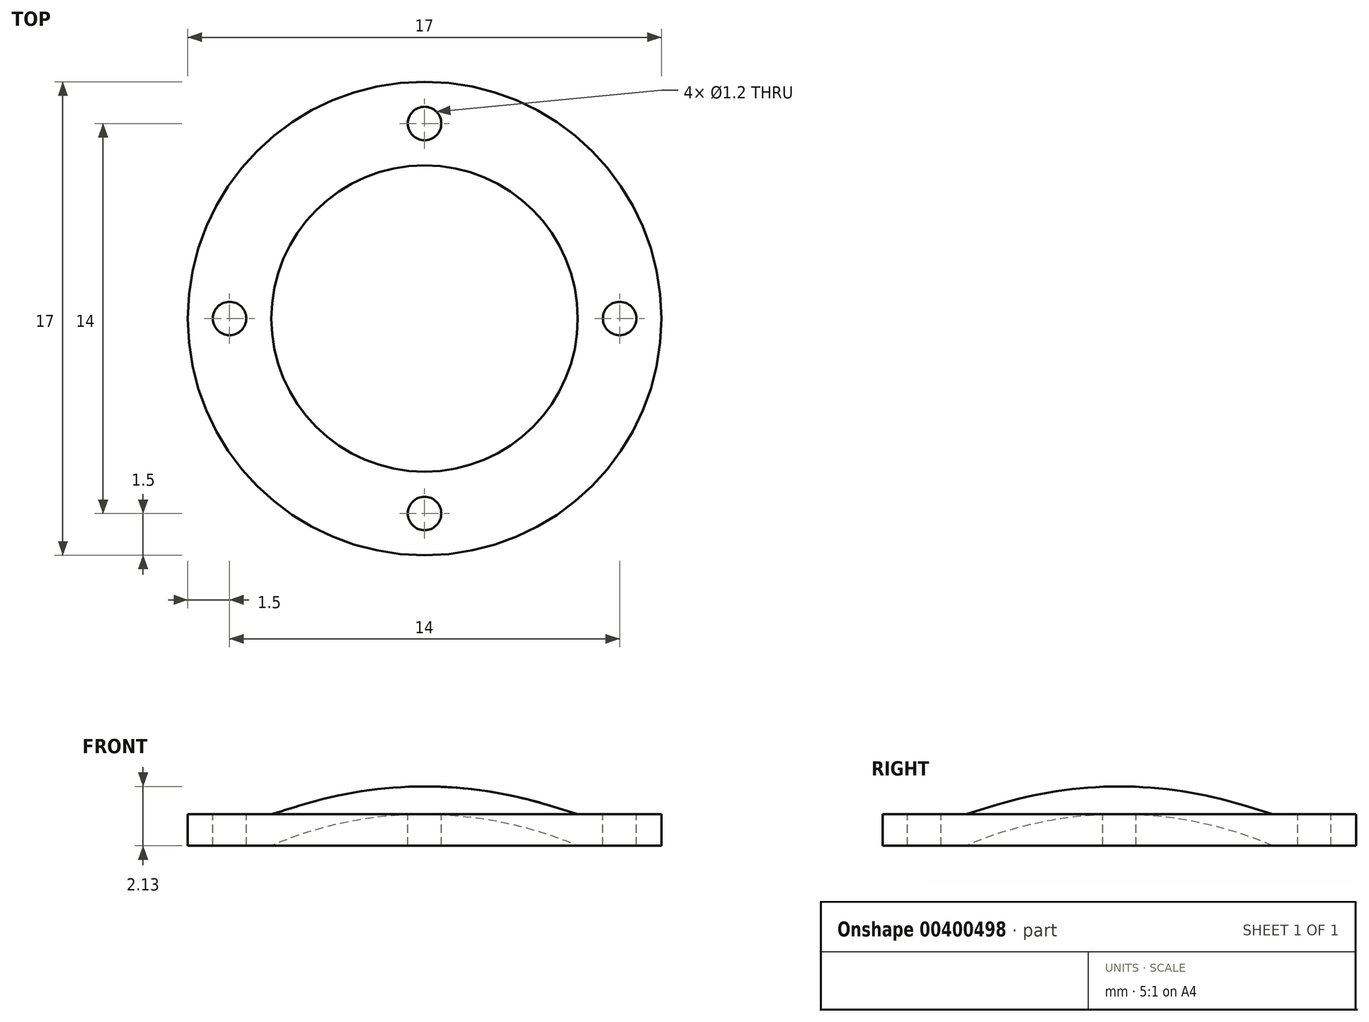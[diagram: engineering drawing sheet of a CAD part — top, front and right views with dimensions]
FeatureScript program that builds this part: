
annotation { "Feature Type Name" : "Feature", "Feature Type Description" : "" }
export const myFeature = defineFeature(function(context is Context, id is Id, definition is map)
    precondition{}
    {
        {
            var Q0;
            Q0=qCreatedBy(makeId("Front.planeOp"),FACE);
            var sketch = newSketch(context, id + "F0", { "sketchPlane" : qUnion([Q0])});
            skLineSegment(sketch, "E0", {"start": v(5.5, 2.87) * mm, "end": v(8.5, 2.87) * mm});
            skLineSegment(sketch, "E1", {"start": v(8.5, 4) * mm, "end": v(5.5, 4) * mm});
            skLineSegment(sketch, "E2", {"start": v(5.5, 4) * mm, "end": v(4.47, 4.32) * mm});
            skArc(sketch, "E3", {"start": v(4.47, 4.32) * mm, "mid": v(2.26, 4.83) * mm, "end": v(0, 5) * mm});
            skLineSegment(sketch, "E4", {"start": v(0, 4) * mm, "end": v(0, 5) * mm});
            skArc(sketch, "E5", {"start": v(5.5, 2.87) * mm, "mid": v(2.8, 3.72) * mm, "end": v(0, 4) * mm});
            skPoint(sketch, "E6.orphan", {"position": v(0, 0) * mm});
            skLineSegment(sketch, "E7", {"start": v(8.5, 4) * mm, "end": v(8.5, 2.87) * mm});
            skSolve(sketch);
        }
        {
            var Q0;
            Q0=makeQuery(id+"F0.imprint","IMPRINT",FACE,{"disambiguationData":[TD([[makeQuery(id+"F0.imprint","IMPRINT",EDGE,{"derivedFrom":sQuery(id+"F0.wireOp",EDGE,"E0")}),1.0]])]});
            var Q1;
            Q1=sQuery(id+"F0.wireOp",EDGE,"E4");
            revolve(context, id + "F1", {"entities" : qUnion([Q0]), "axis" : qUnion([Q1]), "revolveType" : RevolveType.FULL});
        }
        {
            var Q0;
            Q0=makeQuery(id+"F1.opRevolve","SWEPT_FACE",FACE,{"disambiguationData":[OSD([sQuery(id+"F0.wireOp",EDGE,"E1")])]});
            var sketch = newSketch(context, id + "F2", { "sketchPlane" : qUnion([Q0])});
            skCircle(sketch, "E8", {"center": v(0, 7) * mm, "radius": 0.6 * mm});
            skCircle(sketch, "E9.1.0", {"center": v(-7, 0) * mm, "radius": 0.6 * mm});
            skCircle(sketch, "E9.2.0", {"center": v(0, -7) * mm, "radius": 0.6 * mm});
            skCircle(sketch, "E9.3.0", {"center": v(7, 0) * mm, "radius": 0.6 * mm});
            skPoint(sketch, "E9.center", {"position": v(0, 0) * mm});
            skSolve(sketch);
        }
        {
            var Q0;
            Q0 = qSketchRegion(id + "F2", true);
            extrude(context, id + "F3", {"entities" : qUnion([Q0]), "operationType" : NewBodyOperationType.REMOVE, "oppositeDirection" : true, "depth" : 25 * mm});
        }
    });
